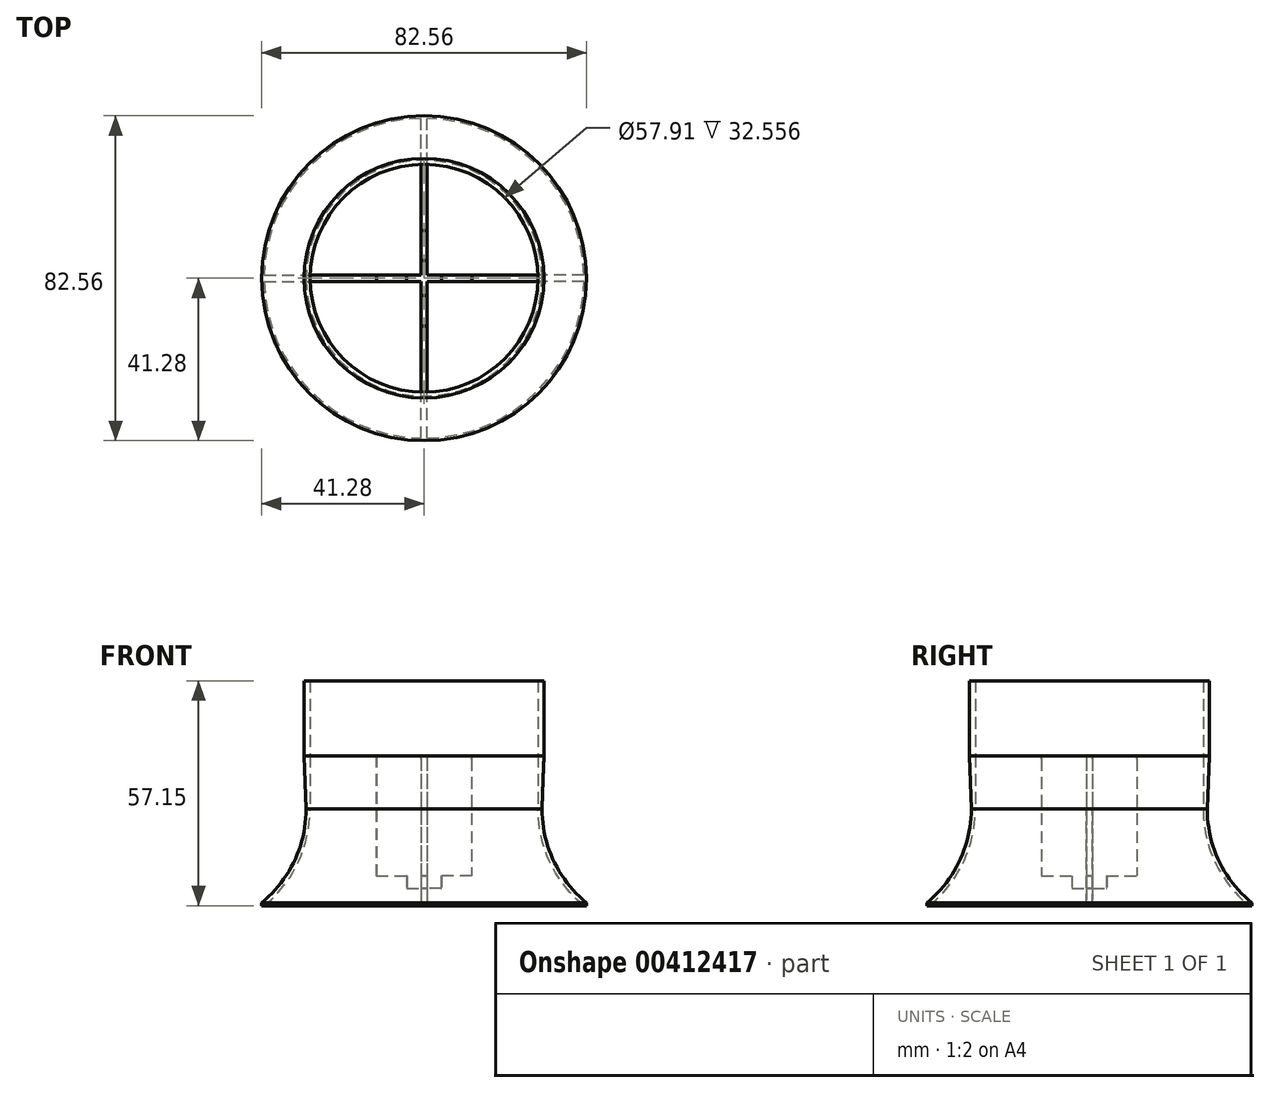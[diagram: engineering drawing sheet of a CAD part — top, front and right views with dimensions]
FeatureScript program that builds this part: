
annotation { "Feature Type Name" : "Feature", "Feature Type Description" : "" }
export const myFeature = defineFeature(function(context is Context, id is Id, definition is map)
    precondition{}
    {
        {
            var Q0;
            Q0=qCreatedBy(makeId("Front.planeOp"),FACE);
            var sketch = newSketch(context, id + "F0", { "sketchPlane" : qUnion([Q0])});
            skLineSegment(sketch, "E0", {"start": v(0, 0) * mm, "end": v(0, 83.31) * mm, "construction": true});
            skLineSegment(sketch, "E1.bottom", {"start": v(28.96, 57.15) * mm, "end": v(29.96, 57.15) * mm});
            skLineSegment(sketch, "E1.left", {"start": v(28.96, 57.15) * mm, "end": v(28.96, 24.6) * mm});
            skLineSegment(sketch, "E1.right", {"start": v(29.96, 57.15) * mm, "end": v(29.96, 24.6) * mm});
            skArc(sketch, "E2", {"start": v(29.96, 24.6) * mm, "mid": v(32.93, 11.4) * mm, "end": v(41.28, 0.76) * mm});
            skArc(sketch, "E3.1", {"start": v(28.96, 24.6) * mm, "mid": v(32.02, 10.98) * mm, "end": v(40.63, 0) * mm});
            skLineSegment(sketch, "E4", {"start": v(40.63, 0) * mm, "end": v(41.28, 0) * mm});
            skLineSegment(sketch, "E5", {"start": v(41.28, 0) * mm, "end": v(41.28, 0.76) * mm});
            skSolve(sketch);
        }
        {
            var Q0;
            Q0 = qSketchRegion(id + "F0", true);
            var Q1;
            Q1=sQuery(id+"F0.wireOp",EDGE,"E0");
            revolve(context, id + "F1", {"entities" : qUnion([Q0]), "axis" : qUnion([Q1]), "revolveType" : RevolveType.FULL});
        }
        {
            var Q0;
            Q0=qCreatedBy(makeId("Front.planeOp"),FACE);
            var sketch = newSketch(context, id + "F2", { "sketchPlane" : qUnion([Q0])});
            skLineSegment(sketch, "E6.bottom", {"start": v(-0.8, 38.1) * mm, "end": v(0.8, 38.1) * mm});
            skLineSegment(sketch, "E6.top", {"start": v(-0.8, 0) * mm, "end": v(0.8, 0) * mm});
            skLineSegment(sketch, "E6.left", {"start": v(-0.8, 38.1) * mm, "end": v(-0.8, 0) * mm});
            skLineSegment(sketch, "E6.right", {"start": v(0.8, 38.1) * mm, "end": v(0.8, 0) * mm});
            skSolve(sketch);
        }
        {
            var Q0;
            Q0 = qSketchRegion(id + "F2", true);
            extrude(context, id + "F3", {"entities" : qUnion([Q0]), "operationType" : NewBodyOperationType.ADD, "endBound" : BoundingType.UP_TO_NEXT, "depth" : 25.4 * mm, "hasSecondDirection" : true, "secondDirectionBound" : SecondDirectionBoundingType.UP_TO_NEXT, "secondDirectionOppositeDirection" : true, "secondDirectionDepth" : 25.4 * mm});
        }
        {
            var Q0;
            Q0=makeQuery(id+"F3.opExtrude","SWEPT_FACE",FACE,{"disambiguationData":[OSD([sQuery(id+"F2.wireOp",EDGE,"E6.right")])]});
            var sketch = newSketch(context, id + "F4", { "sketchPlane" : qUnion([Q0])});
            skLineSegment(sketch, "E7.bottom", {"start": v(-0.8, 38.1) * mm, "end": v(0.8, 38.1) * mm});
            skLineSegment(sketch, "E7.top", {"start": v(-0.8, 0) * mm, "end": v(0.8, 0) * mm});
            skLineSegment(sketch, "E7.left", {"start": v(-0.8, 38.1) * mm, "end": v(-0.8, 0) * mm});
            skLineSegment(sketch, "E7.right", {"start": v(0.8, 38.1) * mm, "end": v(0.8, 0) * mm});
            skSolve(sketch);
        }
        {
            var Q0;
            Q0 = qSketchRegion(id + "F4", true);
            extrude(context, id + "F5", {"entities" : qUnion([Q0]), "operationType" : NewBodyOperationType.ADD, "endBound" : BoundingType.UP_TO_NEXT, "depth" : 25.4 * mm});
        }
        {
            var Q0;
            Q0=makeQuery(id+"F3.opExtrude","SWEPT_FACE",FACE,{"disambiguationData":[OSD([sQuery(id+"F2.wireOp",EDGE,"E6.left")])]});
            var sketch = newSketch(context, id + "F6", { "sketchPlane" : qUnion([Q0])});
            skLineSegment(sketch, "E8.bottom", {"start": v(-0.8, 38.1) * mm, "end": v(0.8, 38.1) * mm});
            skLineSegment(sketch, "E8.top", {"start": v(-0.8, 0) * mm, "end": v(0.8, 0) * mm});
            skLineSegment(sketch, "E8.left", {"start": v(-0.8, 38.1) * mm, "end": v(-0.8, 0) * mm});
            skLineSegment(sketch, "E8.right", {"start": v(0.8, 38.1) * mm, "end": v(0.8, 0) * mm});
            skSolve(sketch);
        }
        {
            var Q0;
            Q0 = qSketchRegion(id + "F6", true);
            extrude(context, id + "F7", {"entities" : qUnion([Q0]), "operationType" : NewBodyOperationType.ADD, "endBound" : BoundingType.UP_TO_NEXT, "depth" : 25.4 * mm});
        }
        {
            var Q0;
            Q0=qCreatedBy(makeId("Front.planeOp"),FACE);
            var sketch = newSketch(context, id + "F8", { "sketchPlane" : qUnion([Q0])});
            skLineSegment(sketch, "E9.bottom", {"start": v(0, 38.1) * mm, "end": v(12.13, 38.1) * mm});
            skLineSegment(sketch, "E9.top", {"start": v(0, 4.44) * mm, "end": v(4.45, 4.44) * mm});
            skLineSegment(sketch, "E9.left", {"start": v(0, 38.1) * mm, "end": v(0, 4.44) * mm});
            skLineSegment(sketch, "E9.right", {"start": v(12.13, 38.1) * mm, "end": v(12.13, 7.62) * mm});
            skLineSegment(sketch, "E10", {"start": v(4.45, 4.44) * mm, "end": v(4.45, 7.62) * mm});
            skLineSegment(sketch, "E11", {"start": v(4.45, 7.62) * mm, "end": v(12.13, 7.62) * mm});
            skSolve(sketch);
        }
        {
            var Q0;
            Q0 = qSketchRegion(id + "F8", true);
            var Q1;
            Q1=sQuery(id+"F8.wireOp",EDGE,"E9.left");
            revolve(context, id + "F9", {"operationType" : NewBodyOperationType.REMOVE, "entities" : qUnion([Q0]), "axis" : qUnion([Q1]), "revolveType" : RevolveType.FULL, "oppositeDirection" : true});
        }
        {
            var Q0;
            {var subQ0=sQuery(id+"F8.wireOp",EDGE,"E9.right");Q0=makeQuery(id+"F9.boolean.opBoolean","COPY",EDGE,{"disambiguationData":[TD([makeQuery(id+"F3.opExtrude","SWEPT_FACE",FACE,{"disambiguationData":[OSD([sQuery(id+"F2.wireOp",EDGE,"E6.bottom")])]}),makeQuery(id+"F3.opExtrude","SWEPT_FACE",FACE,{"disambiguationData":[OSD([sQuery(id+"F2.wireOp",EDGE,"E6.left")])]}),makeQuery(id+"F3.opExtrude","SWEPT_FACE",FACE,{"disambiguationData":[OSD([sQuery(id+"F2.wireOp",EDGE,"E6.right")])]}),makeQuery(id+"F5.opExtrude","SWEPT_FACE",FACE,{"disambiguationData":[OSD([sQuery(id+"F4.wireOp",EDGE,"E7.bottom")])]}),makeQuery(id+"F7.opExtrude","SWEPT_FACE",FACE,{"disambiguationData":[OSD([sQuery(id+"F6.wireOp",EDGE,"E8.bottom")])]}),makeQuery(id+"F9.opRevolve","SWEPT_FACE",FACE,{"disambiguationData":[OSD([subQ0])]})]),OD(0.0)],"derivedFrom":makeQuery(id+"F9.opRevolve","SWEPT_EDGE",EDGE,{"disambiguationData":[OSD([sQuery(id+"F8.wireOp",EDGE,"E9.bottom"),subQ0])]})});}
            var Q1;
            {var subQ0=sQuery(id+"F8.wireOp",EDGE,"E9.right");Q1=makeQuery(id+"F9.boolean.opBoolean","COPY",EDGE,{"disambiguationData":[TD([makeQuery(id+"F3.opExtrude","SWEPT_FACE",FACE,{"disambiguationData":[OSD([sQuery(id+"F2.wireOp",EDGE,"E6.bottom")])]}),makeQuery(id+"F5.opExtrude","SWEPT_FACE",FACE,{"disambiguationData":[OSD([sQuery(id+"F4.wireOp",EDGE,"E7.bottom")])]}),makeQuery(id+"F5.opExtrude","SWEPT_FACE",FACE,{"disambiguationData":[OSD([sQuery(id+"F4.wireOp",EDGE,"E7.left")])]}),makeQuery(id+"F5.opExtrude","SWEPT_FACE",FACE,{"disambiguationData":[OSD([sQuery(id+"F4.wireOp",EDGE,"E7.right")])]}),makeQuery(id+"F7.opExtrude","SWEPT_FACE",FACE,{"disambiguationData":[OSD([sQuery(id+"F6.wireOp",EDGE,"E8.bottom")])]}),makeQuery(id+"F9.opRevolve","SWEPT_FACE",FACE,{"disambiguationData":[OSD([subQ0])]})])],"derivedFrom":makeQuery(id+"F9.opRevolve","SWEPT_EDGE",EDGE,{"disambiguationData":[OSD([sQuery(id+"F8.wireOp",EDGE,"E9.bottom"),subQ0])]})});}
            var Q2;
            {var subQ0=sQuery(id+"F8.wireOp",EDGE,"E9.right");Q2=makeQuery(id+"F9.boolean.opBoolean","COPY",EDGE,{"disambiguationData":[TD([makeQuery(id+"F3.opExtrude","SWEPT_FACE",FACE,{"disambiguationData":[OSD([sQuery(id+"F2.wireOp",EDGE,"E6.bottom")])]}),makeQuery(id+"F3.opExtrude","SWEPT_FACE",FACE,{"disambiguationData":[OSD([sQuery(id+"F2.wireOp",EDGE,"E6.left")])]}),makeQuery(id+"F3.opExtrude","SWEPT_FACE",FACE,{"disambiguationData":[OSD([sQuery(id+"F2.wireOp",EDGE,"E6.right")])]}),makeQuery(id+"F5.opExtrude","SWEPT_FACE",FACE,{"disambiguationData":[OSD([sQuery(id+"F4.wireOp",EDGE,"E7.bottom")])]}),makeQuery(id+"F7.opExtrude","SWEPT_FACE",FACE,{"disambiguationData":[OSD([sQuery(id+"F6.wireOp",EDGE,"E8.bottom")])]}),makeQuery(id+"F9.opRevolve","SWEPT_FACE",FACE,{"disambiguationData":[OSD([subQ0])]})]),OD(1.0)],"derivedFrom":makeQuery(id+"F9.opRevolve","SWEPT_EDGE",EDGE,{"disambiguationData":[OSD([sQuery(id+"F8.wireOp",EDGE,"E9.bottom"),subQ0])]})});}
            var Q3;
            {var subQ0=sQuery(id+"F8.wireOp",EDGE,"E9.right");Q3=makeQuery(id+"F9.boolean.opBoolean","COPY",EDGE,{"disambiguationData":[TD([makeQuery(id+"F3.opExtrude","SWEPT_FACE",FACE,{"disambiguationData":[OSD([sQuery(id+"F2.wireOp",EDGE,"E6.bottom")])]}),makeQuery(id+"F5.opExtrude","SWEPT_FACE",FACE,{"disambiguationData":[OSD([sQuery(id+"F4.wireOp",EDGE,"E7.bottom")])]}),makeQuery(id+"F7.opExtrude","SWEPT_FACE",FACE,{"disambiguationData":[OSD([sQuery(id+"F6.wireOp",EDGE,"E8.bottom")])]}),makeQuery(id+"F7.opExtrude","SWEPT_FACE",FACE,{"disambiguationData":[OSD([sQuery(id+"F6.wireOp",EDGE,"E8.left")])]}),makeQuery(id+"F7.opExtrude","SWEPT_FACE",FACE,{"disambiguationData":[OSD([sQuery(id+"F6.wireOp",EDGE,"E8.right")])]}),makeQuery(id+"F9.opRevolve","SWEPT_FACE",FACE,{"disambiguationData":[OSD([subQ0])]})])],"derivedFrom":makeQuery(id+"F9.opRevolve","SWEPT_EDGE",EDGE,{"disambiguationData":[OSD([sQuery(id+"F8.wireOp",EDGE,"E9.bottom"),subQ0])]})});}
            fillet(context, id + "F10", {"entities" : qUnion([Q0, Q1, Q2, Q3]), "radius" : 0.79 * mm, "tangentPropagation" : true, "allowEdgeOverflow" : false});
        }
        {
            var Q0;
            Q0=qCreatedBy(makeId("Front.planeOp"),FACE);
            var sketch = newSketch(context, id + "F11", { "sketchPlane" : qUnion([Q0])});
            skLineSegment(sketch, "E12", {"start": v(-29.96, 24.6) * mm, "end": v(-30.46, 38.1) * mm});
            skLineSegment(sketch, "E13", {"start": v(-30.46, 38.1) * mm, "end": v(-30.46, 57.15) * mm});
            skLineSegment(sketch, "E14", {"start": v(-30.46, 57.15) * mm, "end": v(-29.96, 57.15) * mm});
            skLineSegment(sketch, "E15", {"start": v(-29.96, 24.6) * mm, "end": v(-29.96, 57.15) * mm});
            skSolve(sketch);
        }
        {
            var Q0;
            Q0 = qSketchRegion(id + "F11", true);
            var Q1;
            Q1=makeQuery(id+"F1.opRevolve","SWEPT_FACE",FACE,{"disambiguationData":[OSD([sQuery(id+"F0.wireOp",EDGE,"E1.right")])]});
            revolve(context, id + "F12", {"operationType" : NewBodyOperationType.ADD, "entities" : qUnion([Q0]), "axis" : qUnion([Q1]), "revolveType" : RevolveType.FULL});
        }
    });
